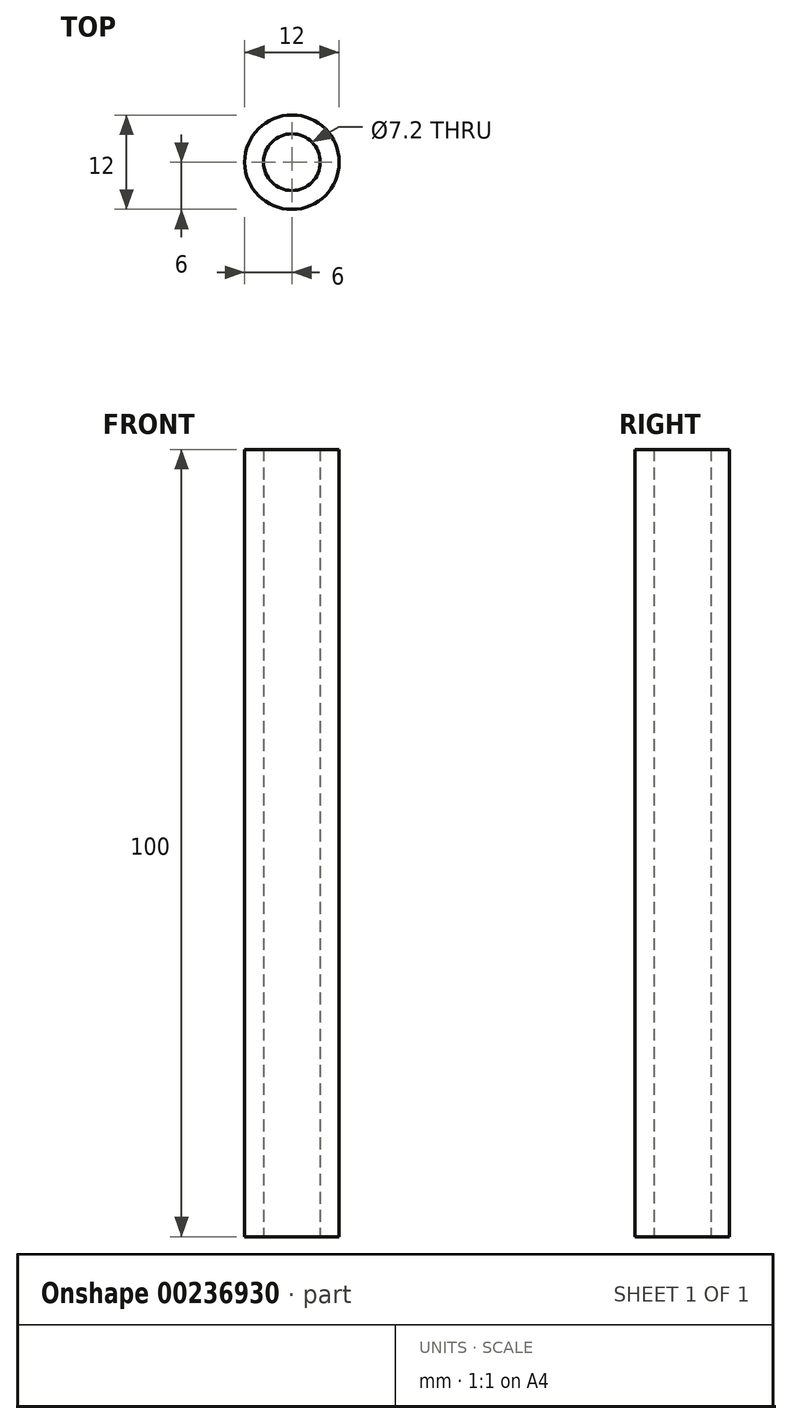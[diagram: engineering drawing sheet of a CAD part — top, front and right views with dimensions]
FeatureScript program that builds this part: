
annotation { "Feature Type Name" : "Feature", "Feature Type Description" : "" }
export const myFeature = defineFeature(function(context is Context, id is Id, definition is map)
    precondition{}
    {
        {
            var Q0;
            Q0=qCreatedBy(makeId("Top.planeOp"),FACE);
            var sketch = newSketch(context, id + "F0", { "sketchPlane" : qUnion([Q0])});
            skCircle(sketch, "E0", {"center": v(0, 0) * mm, "radius": 6 * mm});
            skCircle(sketch, "E1", {"center": v(0, 0) * mm, "radius": 3.6 * mm});
            skSolve(sketch);
        }
        {
            var Q0;
            Q0 = qSketchRegion(id + "F0", true);
            extrude(context, id + "F1", {"entities" : qUnion([Q0]), "depth" : 100 * mm});
        }
    });
